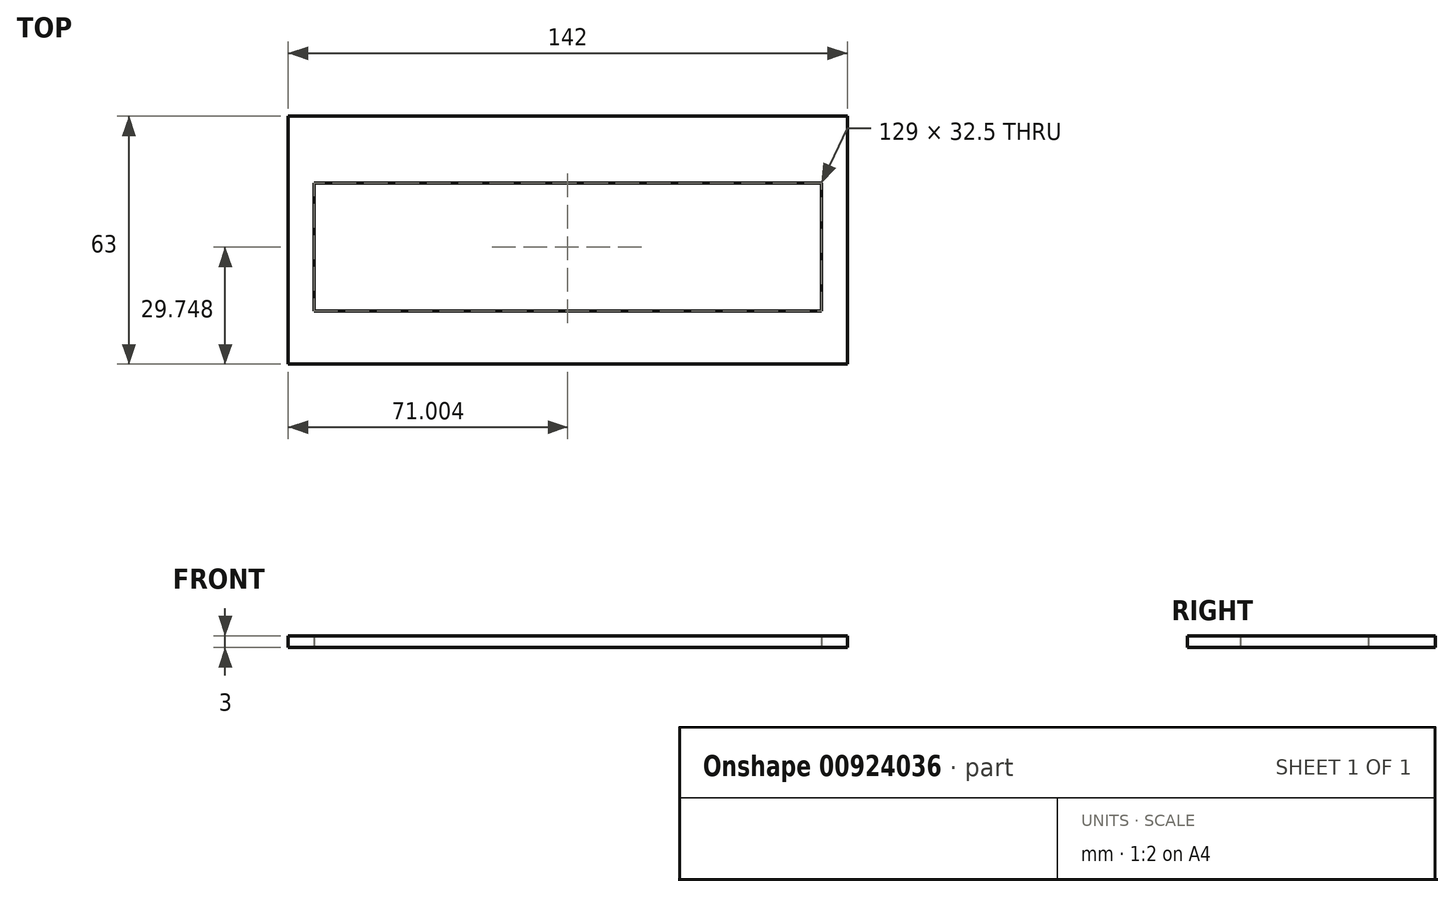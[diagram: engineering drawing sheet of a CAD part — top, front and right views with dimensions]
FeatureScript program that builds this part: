
annotation { "Feature Type Name" : "Feature", "Feature Type Description" : "" }
export const myFeature = defineFeature(function(context is Context, id is Id, definition is map)
    precondition{}
    {
        {
            var Q0;
            Q0=qCreatedBy(makeId("Top.planeOp"),FACE);
            var sketch = newSketch(context, id + "F0", { "sketchPlane" : qUnion([Q0])});
            skLineSegment(sketch, "E0.bottom", {"start": v(-85.13, 56.82) * mm, "end": v(-227.13, 56.82) * mm});
            skLineSegment(sketch, "E0.top", {"start": v(-85.13, 119.82) * mm, "end": v(-227.13, 119.82) * mm});
            skLineSegment(sketch, "E0.left", {"start": v(-85.13, 56.82) * mm, "end": v(-85.13, 119.82) * mm});
            skLineSegment(sketch, "E0.right", {"start": v(-227.13, 56.82) * mm, "end": v(-227.13, 119.82) * mm});
            skPoint(sketch, "E0.middle", {"position": v(-156.13, 88.32) * mm});
            skLineSegment(sketch, "E1.bottom", {"start": v(-91.63, 70.32) * mm, "end": v(-220.63, 70.32) * mm});
            skLineSegment(sketch, "E1.top", {"start": v(-91.63, 102.82) * mm, "end": v(-220.63, 102.82) * mm});
            skLineSegment(sketch, "E1.left", {"start": v(-91.63, 70.32) * mm, "end": v(-91.63, 102.82) * mm});
            skLineSegment(sketch, "E1.right", {"start": v(-220.63, 70.32) * mm, "end": v(-220.63, 102.82) * mm});
            skPoint(sketch, "E1.middle", {"position": v(-156.13, 86.57) * mm});
            skSolve(sketch);
        }
        {
            var Q0;
            Q0 = qSketchRegion(id + "F0", true);
            extrude(context, id + "F1", {"entities" : qUnion([Q0]), "depth" : 3 * mm, "offsetDistance" : 25 * mm});
        }
    });
